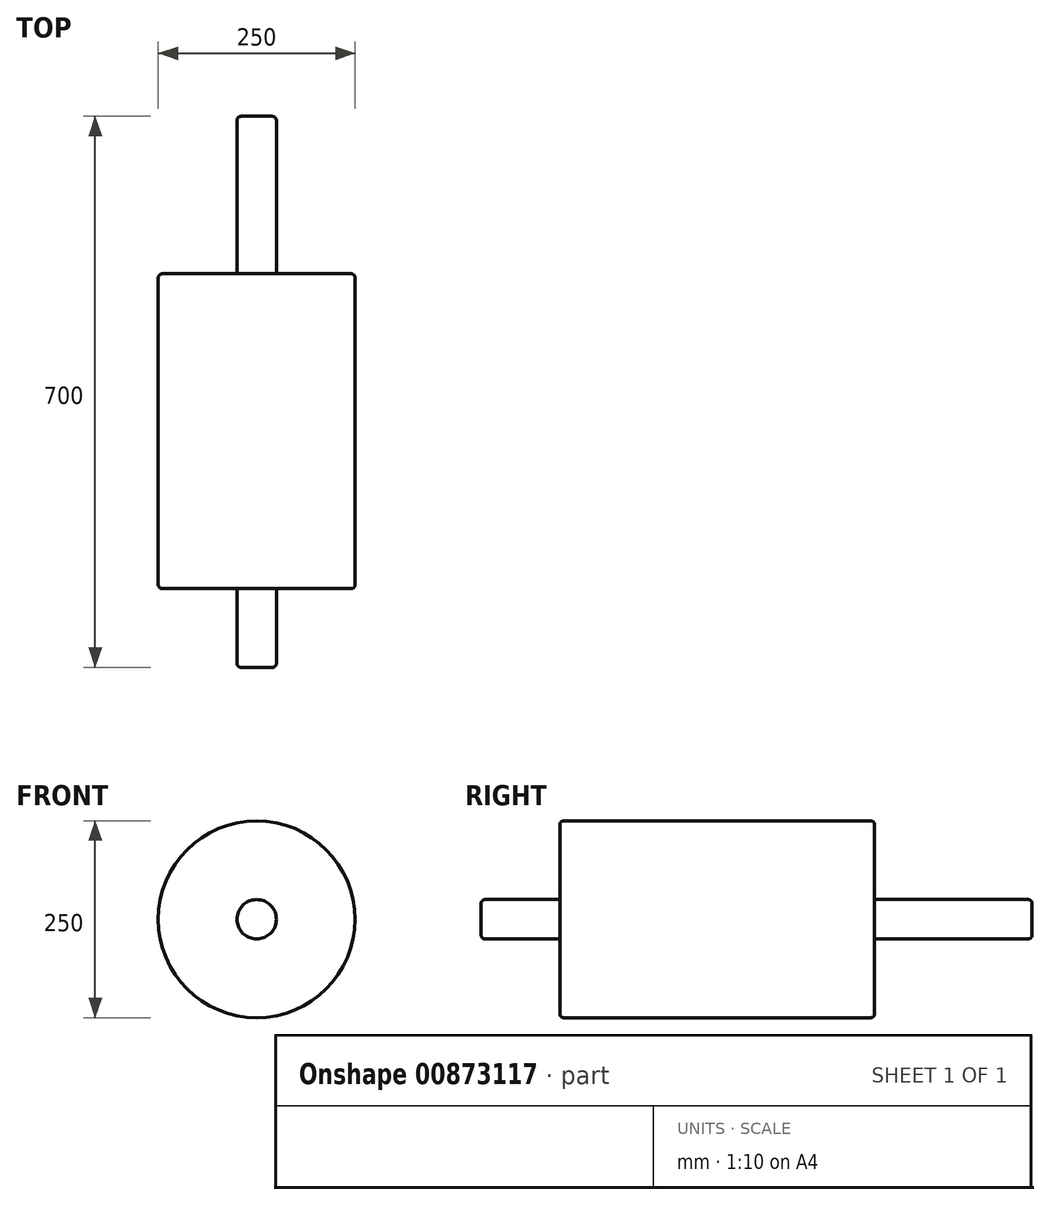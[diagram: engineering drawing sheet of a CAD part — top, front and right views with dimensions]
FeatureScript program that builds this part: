
annotation { "Feature Type Name" : "Feature", "Feature Type Description" : "" }
export const myFeature = defineFeature(function(context is Context, id is Id, definition is map)
    precondition{}
    {
        {
            var Q0;
            Q0=qCreatedBy(makeId("Front.planeOp"),FACE);
            var sketch = newSketch(context, id + "F0", { "sketchPlane" : qUnion([Q0])});
            skCircle(sketch, "E0", {"center": v(0, 0) * mm, "radius": 125 * mm});
            skSolve(sketch);
        }
        {
            var Q0;
            Q0 = qSketchRegion(id + "F0", true);
            var Q1;
            Q1=makeQuery(id+"F0.imprint","IMPRINT",FACE,{"disambiguationData":[TD([[makeQuery(id+"F0.imprint","IMPRINT",EDGE,{"derivedFrom":sQuery(id+"F0.wireOp",EDGE,"E0")}),1.0]])]});
            extrude(context, id + "F1", {"entities" : qUnion([Q0, Q1]), "depth" : 400 * mm, "offsetDistance" : 25 * mm});
        }
        {
            var Q0;
            Q0=makeQuery(id+"F1.opExtrude","CAP_FACE",FACE,{"disambiguationData":[OSD([sQuery(id+"F0.wireOp",EDGE,"E0")])],"isStart":true});
            var sketch = newSketch(context, id + "F2", { "sketchPlane" : qUnion([Q0])});
            skSolve(sketch);
        }
        {
            var Q0;
            Q0 = qSketchRegion(id + "F0", true);
            extrude(context, id + "F3", {"entities" : qUnion([Q0]), "operationType" : NewBodyOperationType.ADD, "depth" : 25 * mm, "offsetDistance" : 25 * mm});
        }
        {
            var Q0;
            Q0=makeQuery(id+"F1.opExtrude","CAP_EDGE",EDGE,{"disambiguationData":[OSD([sQuery(id+"F0.wireOp",EDGE,"E0")])],"isStart":true});
            var Q1;
            Q1=makeQuery(id+"F1.opExtrude","CAP_EDGE",EDGE,{"disambiguationData":[OSD([sQuery(id+"F0.wireOp",EDGE,"E0")])],"isStart":false});
            fillet(context, id + "F4", {"entities" : qUnion([Q0, Q1]), "radius" : 5 * mm, "tangentPropagation" : true, "allowEdgeOverflow" : false});
        }
        {
            var Q0;
            Q0=makeQuery(id+"F1.opExtrude","CAP_FACE",FACE,{"disambiguationData":[OSD([sQuery(id+"F0.wireOp",EDGE,"E0")])],"isStart":false});
            var sketch = newSketch(context, id + "F5", { "sketchPlane" : qUnion([Q0])});
            skCircle(sketch, "E1", {"center": v(0, 0) * mm, "radius": 25 * mm});
            skSolve(sketch);
        }
        {
            var Q0;
            Q0 = qSketchRegion(id + "F5", true);
            extrude(context, id + "F6", {"entities" : qUnion([Q0]), "operationType" : NewBodyOperationType.ADD, "depth" : 100 * mm, "offsetDistance" : 25 * mm});
        }
        {
            var Q0;
            Q0=makeQuery(id+"F6.opExtrude","CAP_EDGE",EDGE,{"disambiguationData":[OSD([sQuery(id+"F5.wireOp",EDGE,"E1")])],"isStart":true});
            var Q1;
            Q1=makeQuery(id+"F6.opExtrude","CAP_EDGE",EDGE,{"disambiguationData":[OSD([sQuery(id+"F5.wireOp",EDGE,"E1")])],"isStart":false});
            fillet(context, id + "F7", {"entities" : qUnion([Q0, Q1]), "radius" : 5 * mm, "tangentPropagation" : true, "allowEdgeOverflow" : false});
        }
        {
            var Q0;
            Q0=makeQuery(id+"F2.imprint","IMPRINT",FACE,{"disambiguationData":[TD([[makeQuery(id+"F2.imprint","IMPRINT",EDGE,{"derivedFrom":makeQuery(id+"F1.opExtrude","CAP_EDGE",EDGE,{"disambiguationData":[OSD([sQuery(id+"F0.wireOp",EDGE,"E0")])],"isStart":true})}),-1.0]])]});
            var sketch = newSketch(context, id + "F8", { "sketchPlane" : qUnion([Q0])});
            skCircle(sketch, "E2", {"center": v(0, 0) * mm, "radius": 25 * mm});
            skSolve(sketch);
        }
        {
            var Q0;
            Q0 = qSketchRegion(id + "F8", true);
            extrude(context, id + "F9", {"entities" : qUnion([Q0]), "operationType" : NewBodyOperationType.ADD, "depth" : 200 * mm, "offsetDistance" : 25 * mm});
        }
        {
            var Q0;
            Q0=makeQuery(id+"F9.opExtrude","CAP_EDGE",EDGE,{"disambiguationData":[OSD([sQuery(id+"F8.wireOp",EDGE,"E2")])],"isStart":true});
            var Q1;
            Q1=makeQuery(id+"F9.opExtrude","CAP_EDGE",EDGE,{"disambiguationData":[OSD([sQuery(id+"F8.wireOp",EDGE,"E2")])],"isStart":false});
            fillet(context, id + "F10", {"entities" : qUnion([Q0, Q1]), "radius" : 5 * mm, "tangentPropagation" : true, "allowEdgeOverflow" : false});
        }
    });
